# Revit family: Electronics_Commercial-Audio_Biamp_Bridgeable-Power-Amplifier_PA240BP
name_source: partatom
category: Communication Devices
units: mm (PartAtom-declared; Revit-internal decimal feet)

## family parameters
Cut with Voids When Loaded = No
Host = Face
Maintain Annotation Orientation = No
OmniClass Number = 23.85.10.11.14.14.17
OmniClass Title = Sound Amplifiers
Part Type = Normal
Room Calculation Point = No
Round Connector Dimension = Use Diameter
Shared = No

## types (1)
- PA2240BP
    Apparent Load = 1050 VA
    Connector Description = Power supply
    Default Elevation = 1219.2 mm  [stored 4 ft]
    Depth = 430 mm
    Description = PA2240BP 2-Channel Bridgeable Power Amplifier
    Height = 90 mm  [stored 0.295276 ft]
    Housing Material = Biamp - Metal - Black
    Installation Type 1 = Rack mounting
    Installation Type 2 = Surface mounting
    Manufacturer = Biamp
    Max Power Consumption = 1050 W
    Model = PA2240BP
    Number of Poles = 1
    Power Factor = 1
    Product Documentation Link = https://downloads.biamp.com
    Product Page URL = https://www.biamp.com
    Product data url = https://bimobject.com
    URL = https://www.biamp.com
    Version = 1
    Voltage = 240 V
    Weight = 24.10 kgf
    Width = 483 mm

note: [stored X ft] marks values corroborated as IEEE doubles in the binary element streams (Revit-internal decimal feet)

## geometry (parser evidence)
native form markers: Sweep x7
no freeform markers — native parametric forms only
